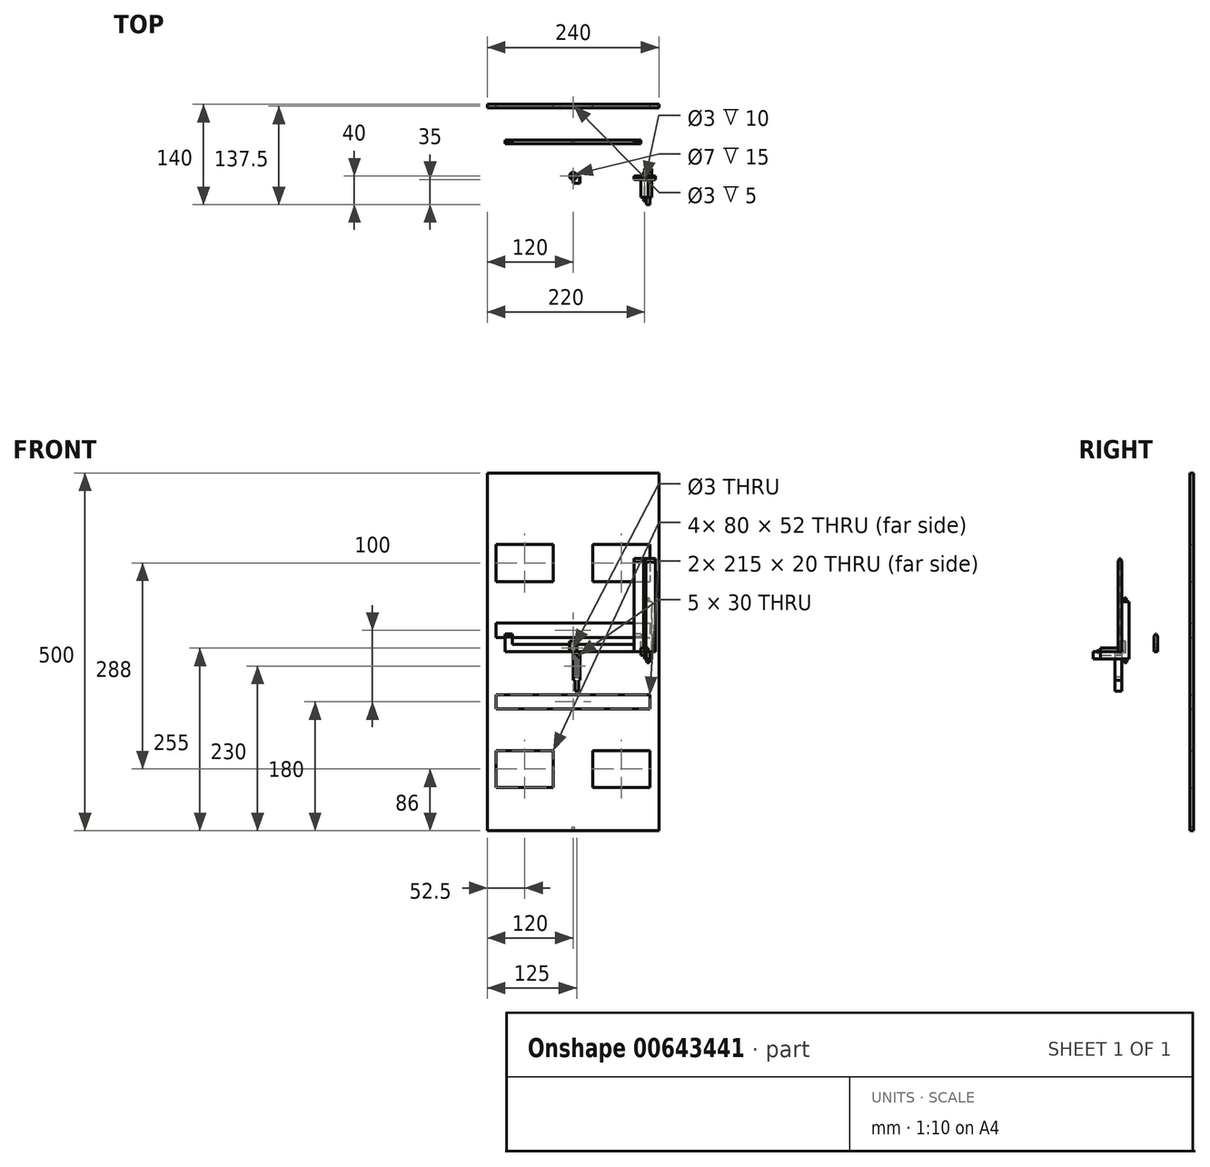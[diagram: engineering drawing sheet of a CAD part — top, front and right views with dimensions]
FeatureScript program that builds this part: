
annotation { "Feature Type Name" : "Feature", "Feature Type Description" : "" }
export const myFeature = defineFeature(function(context is Context, id is Id, definition is map)
    precondition{}
    {
        {
            var Q0;
            Q0=qCreatedBy(makeId("Front.planeOp"),FACE);
            var sketch = newSketch(context, id + "F0", { "sketchPlane" : qUnion([Q0])});
            skLineSegment(sketch, "E0", {"start": v(0, 0) * mm, "end": v(95, 0) * mm});
            skLineSegment(sketch, "E1", {"start": v(95, 0) * mm, "end": v(95, 25) * mm});
            skLineSegment(sketch, "E2", {"start": v(95, 25) * mm, "end": v(85, 25) * mm});
            skLineSegment(sketch, "E3", {"start": v(85, 25) * mm, "end": v(85, 10) * mm});
            skLineSegment(sketch, "E4", {"start": v(85, 10) * mm, "end": v(0, 10) * mm});
            skLineSegment(sketch, "E5.MirrorCS", {"start": v(-85, 25) * mm, "end": v(-85, 10) * mm});
            skLineSegment(sketch, "E6.MirrorCS", {"start": v(-85, 10) * mm, "end": v(0, 10) * mm});
            skLineSegment(sketch, "E7.MirrorCS", {"start": v(-95, 0) * mm, "end": v(-95, 25) * mm});
            skLineSegment(sketch, "E8.MirrorCS", {"start": v(0, 0) * mm, "end": v(-95, 0) * mm});
            skLineSegment(sketch, "E9.MirrorCS", {"start": v(-95, 25) * mm, "end": v(-85, 25) * mm});
            skCircle(sketch, "E10", {"center": v(0, 5) * mm, "radius": 1.5 * mm});
            skSolve(sketch);
        }
        {
            var Q0;
            Q0=makeQuery(id+"F0.imprint","IMPRINT",FACE,{"disambiguationData":[TD([[makeQuery(id+"F0.imprint","IMPRINT",EDGE,{"derivedFrom":sQuery(id+"F0.wireOp",EDGE,"E0")}),1.0]])]});
            extrude(context, id + "F1", {"entities" : qUnion([Q0]), "depth" : 5 * mm, "offsetDistance" : 25 * mm});
        }
        {
            var Q0;
            Q0=makeQuery(id+"F1.opExtrude","CAP_EDGE",EDGE,{"disambiguationData":[OSD([sQuery(id+"F0.wireOp",EDGE,"E2")])],"isStart":false});
            var Q1;
            Q1=makeQuery(id+"F1.opExtrude","CAP_EDGE",EDGE,{"disambiguationData":[OSD([sQuery(id+"F0.wireOp",EDGE,"E9.MirrorCS")])],"isStart":false});
            var Q2;
            Q2=makeQuery(id+"F1.opExtrude","CAP_EDGE",EDGE,{"disambiguationData":[OSD([sQuery(id+"F0.wireOp",EDGE,"E2")])],"isStart":true});
            var Q3;
            Q3=makeQuery(id+"F1.opExtrude","CAP_EDGE",EDGE,{"disambiguationData":[OSD([sQuery(id+"F0.wireOp",EDGE,"E9.MirrorCS")])],"isStart":true});
            chamfer(context, id + "F2", {"entities" : qUnion([Q0, Q1, Q2, Q3]), "chamferType" : ChamferType.TWO_OFFSETS, "width1" : 4 * mm, "oppositeDirection" : false, "width2" : 2 * mm, "tangentPropagation" : true});
        }
        {
            var Q0;
            Q0=makeQuery(id+"F1.opExtrude","SWEPT_BODY",BODY,{"disambiguationData":[OSD([sQuery(id+"F0.wireOp",EDGE,"E0"),sQuery(id+"F0.wireOp",EDGE,"E1"),sQuery(id+"F0.wireOp",EDGE,"E2"),sQuery(id+"F0.wireOp",EDGE,"E3"),sQuery(id+"F0.wireOp",EDGE,"E4"),sQuery(id+"F0.wireOp",EDGE,"E5.MirrorCS"),sQuery(id+"F0.wireOp",EDGE,"E6.MirrorCS"),sQuery(id+"F0.wireOp",EDGE,"E7.MirrorCS"),sQuery(id+"F0.wireOp",EDGE,"E8.MirrorCS"),sQuery(id+"F0.wireOp",EDGE,"E9.MirrorCS")])]});
            transform(context, id + "F3", {"entities" : qUnion([Q0]), "transformType" : TransformType.TRANSLATION_3D, "dx" : 0 * mm, "dy" : 50 * mm, "dz" : 0 * mm, "makeCopy" : false});
        }
        {
            var Q0;
            Q0=qCreatedBy(makeId("Front.planeOp"),FACE);
            var sketch = newSketch(context, id + "F4", { "sketchPlane" : qUnion([Q0])});
            skLineSegment(sketch, "E11.bottom", {"start": v(-15, 0) * mm, "end": v(15, 0) * mm});
            skLineSegment(sketch, "E11.top", {"start": v(-15, 130) * mm, "end": v(15, 130) * mm});
            skLineSegment(sketch, "E11.left", {"start": v(-15, 0) * mm, "end": v(-15, 130) * mm});
            skLineSegment(sketch, "E11.right", {"start": v(15, 0) * mm, "end": v(15, 130) * mm});
            skCircle(sketch, "E12", {"center": v(0, 5) * mm, "radius": 1.5 * mm});
            skSolve(sketch);
        }
        {
            var Q0;
            Q0=makeQuery(id+"F4.imprint","IMPRINT",FACE,{"disambiguationData":[TD([[makeQuery(id+"F4.imprint","IMPRINT",EDGE,{"derivedFrom":sQuery(id+"F4.wireOp",EDGE,"E11.bottom")}),1.0]])]});
            extrude(context, id + "F5", {"entities" : qUnion([Q0]), "depth" : 5 * mm, "offsetDistance" : 25 * mm});
        }
        {
            var Q0;
            Q0=makeQuery(id+"F5.opExtrude","CAP_EDGE",EDGE,{"disambiguationData":[OSD([sQuery(id+"F4.wireOp",EDGE,"E11.top")])],"isStart":false});
            var Q1;
            Q1=makeQuery(id+"F5.opExtrude","CAP_EDGE",EDGE,{"disambiguationData":[OSD([sQuery(id+"F4.wireOp",EDGE,"E11.top")])],"isStart":true});
            chamfer(context, id + "F6", {"entities" : qUnion([Q0, Q1]), "chamferType" : ChamferType.TWO_OFFSETS, "width1" : 5 * mm, "oppositeDirection" : true, "width2" : 2 * mm, "tangentPropagation" : true});
        }
        {
            var Q0;
            Q0=qCreatedBy(makeId("Front.planeOp"),FACE);
            var sketch = newSketch(context, id + "F7", { "sketchPlane" : qUnion([Q0])});
            skLineSegment(sketch, "E13.bottom", {"start": v(-5, 5) * mm, "end": v(5, 5) * mm});
            skLineSegment(sketch, "E13.top", {"start": v(-5, -5) * mm, "end": v(5, -5) * mm});
            skLineSegment(sketch, "E13.left", {"start": v(-5, 5) * mm, "end": v(-5, -5) * mm});
            skLineSegment(sketch, "E13.right", {"start": v(5, 5) * mm, "end": v(5, -5) * mm});
            skSolve(sketch);
        }
        {
            var Q0;
            Q0=makeQuery(id+"F7.imprint","IMPRINT",FACE,{"disambiguationData":[TD([[makeQuery(id+"F7.imprint","IMPRINT",EDGE,{"derivedFrom":sQuery(id+"F7.wireOp",EDGE,"E13.bottom")}),-1.0]])]});
            extrude(context, id + "F8", {"entities" : qUnion([Q0]), "depth" : 30 * mm, "offsetDistance" : 25 * mm});
        }
        {
            var Q0;
            Q0=makeQuery(id+"F8.opExtrude","CAP_FACE",FACE,{"disambiguationData":[OSD([sQuery(id+"F7.wireOp",EDGE,"E13.bottom"),sQuery(id+"F7.wireOp",EDGE,"E13.top"),sQuery(id+"F7.wireOp",EDGE,"E13.left"),sQuery(id+"F7.wireOp",EDGE,"E13.right")])],"isStart":false});
            var sketch = newSketch(context, id + "F9", { "sketchPlane" : qUnion([Q0])});
            skCircle(sketch, "E14", {"center": v(0, 0) * mm, "radius": 1.5 * mm});
            skSolve(sketch);
        }
        {
            var Q0;
            Q0=makeQuery(id+"F9.imprint","IMPRINT",FACE,{"disambiguationData":[TD([[makeQuery(id+"F9.imprint","IMPRINT",EDGE,{"derivedFrom":sQuery(id+"F9.wireOp",EDGE,"E14")}),1.0]])]});
            extrude(context, id + "F10", {"entities" : qUnion([Q0]), "operationType" : NewBodyOperationType.ADD, "depth" : 5 * mm, "offsetDistance" : 25 * mm});
        }
        {
            var Q0;
            Q0=makeQuery(id+"F8.opExtrude","CAP_FACE",FACE,{"disambiguationData":[OSD([sQuery(id+"F7.wireOp",EDGE,"E13.bottom"),sQuery(id+"F7.wireOp",EDGE,"E13.top"),sQuery(id+"F7.wireOp",EDGE,"E13.left"),sQuery(id+"F7.wireOp",EDGE,"E13.right")])],"isStart":true});
            var sketch = newSketch(context, id + "F11", { "sketchPlane" : qUnion([Q0])});
            skCircle(sketch, "E15", {"center": v(0, 0) * mm, "radius": 1.5 * mm});
            skSolve(sketch);
        }
        {
            var Q0;
            Q0=makeQuery(id+"F11.imprint","IMPRINT",FACE,{"disambiguationData":[TD([[makeQuery(id+"F11.imprint","IMPRINT",EDGE,{"derivedFrom":sQuery(id+"F11.wireOp",EDGE,"E15")}),1.0]])]});
            extrude(context, id + "F12", {"entities" : qUnion([Q0]), "operationType" : NewBodyOperationType.ADD, "depth" : 5 * mm, "offsetDistance" : 25 * mm});
        }
        {
            var Q0;
            Q0=qCreatedBy(makeId("Right.planeOp"),FACE);
            var sketch = newSketch(context, id + "F13", { "sketchPlane" : qUnion([Q0])});
            skLineSegment(sketch, "E16", {"start": v(0, 70) * mm, "end": v(10, 70) * mm});
            skLineSegment(sketch, "E17", {"start": v(10, 70) * mm, "end": v(10, -10) * mm});
            skLineSegment(sketch, "E18", {"start": v(10, -10) * mm, "end": v(-30, -10) * mm});
            skLineSegment(sketch, "E19", {"start": v(-30, -10) * mm, "end": v(-30, 0) * mm});
            skLineSegment(sketch, "E20", {"start": v(-30, 0) * mm, "end": v(0, 0) * mm});
            skLineSegment(sketch, "E21", {"start": v(0, 0) * mm, "end": v(0, 15) * mm});
            skLineSegment(sketch, "E22", {"start": v(0, 20) * mm, "end": v(-5, 20) * mm});
            skLineSegment(sketch, "E23", {"start": v(-5, 20) * mm, "end": v(-5, 15) * mm});
            skLineSegment(sketch, "E24", {"start": v(-5, 15) * mm, "end": v(0, 15) * mm});
            skLineSegment(sketch, "E25.trimOffspring", {"start": v(0, 20) * mm, "end": v(0, 70) * mm});
            skSolve(sketch);
        }
        {
            var Q0;
            Q0=makeQuery(id+"F13.imprint","IMPRINT",FACE,{"disambiguationData":[TD([[makeQuery(id+"F13.imprint","IMPRINT",EDGE,{"derivedFrom":sQuery(id+"F13.wireOp",EDGE,"E16")}),-1.0]])]});
            extrude(context, id + "F14", {"entities" : qUnion([Q0]), "depth" : 10 * mm, "offsetDistance" : 25 * mm});
        }
        {
            var Q0;
            Q0=makeQuery(id+"F14.opExtrude","SWEPT_FACE",FACE,{"disambiguationData":[OSD([sQuery(id+"F13.wireOp",EDGE,"E16")])]});
            var sketch = newSketch(context, id + "F15", { "sketchPlane" : qUnion([Q0])});
            skCircle(sketch, "E26", {"center": v(5, 5) * mm, "radius": 1.5 * mm});
            skSolve(sketch);
        }
        {
            var Q0;
            Q0=makeQuery(id+"F15.imprint","IMPRINT",FACE,{"disambiguationData":[TD([[makeQuery(id+"F15.imprint","IMPRINT",EDGE,{"derivedFrom":sQuery(id+"F15.wireOp",EDGE,"E26")}),1.0]])]});
            extrude(context, id + "F16", {"entities" : qUnion([Q0]), "operationType" : NewBodyOperationType.ADD, "depth" : 5 * mm, "offsetDistance" : 25 * mm});
        }
        {
            var Q0;
            Q0=makeQuery(id+"F14.opExtrude","SWEPT_FACE",FACE,{"disambiguationData":[OSD([sQuery(id+"F13.wireOp",EDGE,"E19")])]});
            var sketch = newSketch(context, id + "F17", { "sketchPlane" : qUnion([Q0])});
            skLineSegment(sketch, "E27.bottom", {"start": v(2.5, 0) * mm, "end": v(7.5, 0) * mm});
            skLineSegment(sketch, "E27.top", {"start": v(2.5, -10) * mm, "end": v(7.5, -10) * mm});
            skLineSegment(sketch, "E27.left", {"start": v(2.5, 0) * mm, "end": v(2.5, -10) * mm});
            skLineSegment(sketch, "E27.right", {"start": v(7.5, 0) * mm, "end": v(7.5, -10) * mm});
            skSolve(sketch);
        }
        {
            var Q0;
            Q0=makeQuery(id+"F8.opExtrude","SWEPT_FACE",FACE,{"disambiguationData":[OSD([sQuery(id+"F7.wireOp",EDGE,"E13.top")])]});
            var sketch = newSketch(context, id + "F18", { "sketchPlane" : qUnion([Q0])});
            skCircle(sketch, "E28", {"center": v(0, 5) * mm, "radius": 1.5 * mm});
            skPoint(sketch, "E28.centerSnap0", {"position": v(0, 30) * mm});
            skSolve(sketch);
        }
        {
            var Q0;
            Q0=makeQuery(id+"F18.imprint","IMPRINT",FACE,{"disambiguationData":[TD([[makeQuery(id+"F18.imprint","IMPRINT",EDGE,{"derivedFrom":sQuery(id+"F18.wireOp",EDGE,"E28")}),1.0]])]});
            extrude(context, id + "F19", {"entities" : qUnion([Q0]), "operationType" : NewBodyOperationType.REMOVE, "endBound" : BoundingType.THROUGH_ALL, "oppositeDirection" : true, "depth" : 5 * mm, "offsetDistance" : 25 * mm});
        }
        {
            var Q0;
            Q0=makeQuery(id+"F17.imprint","IMPRINT",FACE,{"disambiguationData":[TD([[makeQuery(id+"F17.imprint","IMPRINT",EDGE,{"derivedFrom":sQuery(id+"F17.wireOp",EDGE,"E27.bottom")}),1.0]])]});
            extrude(context, id + "F20", {"entities" : qUnion([Q0]), "operationType" : NewBodyOperationType.ADD, "depth" : 10 * mm, "offsetDistance" : 25 * mm});
        }
        {
            var Q0;
            Q0=qCreatedBy(makeId("Front.planeOp"),FACE);
            var sketch = newSketch(context, id + "F21", { "sketchPlane" : qUnion([Q0])});
            skLineSegment(sketch, "E29", {"start": v(0, 0) * mm, "end": v(10, 0) * mm});
            skLineSegment(sketch, "E30", {"start": v(10, 0) * mm, "end": v(10, -40) * mm});
            skLineSegment(sketch, "E31", {"start": v(10, -40) * mm, "end": v(7.5, -40) * mm});
            skLineSegment(sketch, "E32", {"start": v(7.5, -40) * mm, "end": v(7.5, -55) * mm});
            skLineSegment(sketch, "E33", {"start": v(7.5, -55) * mm, "end": v(2.5, -55) * mm});
            skLineSegment(sketch, "E34", {"start": v(2.5, -55) * mm, "end": v(2.5, -40) * mm});
            skLineSegment(sketch, "E35", {"start": v(2.5, -40) * mm, "end": v(0, -40) * mm});
            skLineSegment(sketch, "E36", {"start": v(0, -40) * mm, "end": v(0, 0) * mm});
            skLineSegment(sketch, "E37.bottom", {"start": v(2.5, -5) * mm, "end": v(7.5, -5) * mm});
            skLineSegment(sketch, "E37.top", {"start": v(2.5, -35) * mm, "end": v(7.5, -35) * mm});
            skLineSegment(sketch, "E37.left", {"start": v(2.5, -5) * mm, "end": v(2.5, -35) * mm});
            skLineSegment(sketch, "E37.right", {"start": v(7.5, -5) * mm, "end": v(7.5, -35) * mm});
            skSolve(sketch);
        }
        {
            var Q0;
            Q0=makeQuery(id+"F21.imprint","IMPRINT",FACE,{"disambiguationData":[TD([[makeQuery(id+"F21.imprint","IMPRINT",EDGE,{"derivedFrom":sQuery(id+"F21.wireOp",EDGE,"E29")}),-1.0]])]});
            extrude(context, id + "F22", {"entities" : qUnion([Q0]), "depth" : 10 * mm, "offsetDistance" : 25 * mm});
        }
        {
            var Q0;
            Q0=qCreatedBy(makeId("Front.planeOp"),FACE);
            var sketch = newSketch(context, id + "F23", { "sketchPlane" : qUnion([Q0])});
            skLineSegment(sketch, "E38.bottom", {"start": v(-120, 250) * mm, "end": v(120, 250) * mm});
            skLineSegment(sketch, "E38.top", {"start": v(-120, -250) * mm, "end": v(120, -250) * mm});
            skLineSegment(sketch, "E38.left", {"start": v(-120, 250) * mm, "end": v(-120, -250) * mm});
            skLineSegment(sketch, "E38.right", {"start": v(120, 250) * mm, "end": v(120, -250) * mm});
            skLineSegment(sketch, "E39.bottom", {"start": v(-107.5, -138) * mm, "end": v(-27.5, -138) * mm});
            skLineSegment(sketch, "E39.top", {"start": v(-107.5, -190) * mm, "end": v(-27.5, -190) * mm});
            skLineSegment(sketch, "E39.left", {"start": v(-107.5, -138) * mm, "end": v(-107.5, -190) * mm});
            skLineSegment(sketch, "E39.right", {"start": v(-27.5, -138) * mm, "end": v(-27.5, -190) * mm});
            skLineSegment(sketch, "E40.bottom", {"start": v(-107.5, -60) * mm, "end": v(107.5, -60) * mm});
            skLineSegment(sketch, "E40.top", {"start": v(-107.5, -80) * mm, "end": v(107.5, -80) * mm});
            skLineSegment(sketch, "E40.left", {"start": v(-107.5, -60) * mm, "end": v(-107.5, -80) * mm});
            skLineSegment(sketch, "E40.right", {"start": v(107.5, -60) * mm, "end": v(107.5, -80) * mm});
            skLineSegment(sketch, "E41.bottom", {"start": v(27.5, -138) * mm, "end": v(107.5, -138) * mm});
            skLineSegment(sketch, "E41.top", {"start": v(27.5, -190) * mm, "end": v(107.5, -190) * mm});
            skLineSegment(sketch, "E41.left", {"start": v(27.5, -138) * mm, "end": v(27.5, -190) * mm});
            skLineSegment(sketch, "E41.right", {"start": v(107.5, -138) * mm, "end": v(107.5, -190) * mm});
            skLineSegment(sketch, "E42.bottom", {"start": v(-107.5, 40) * mm, "end": v(107.5, 40) * mm});
            skLineSegment(sketch, "E42.top", {"start": v(-107.5, 20) * mm, "end": v(107.5, 20) * mm});
            skLineSegment(sketch, "E42.left", {"start": v(-107.5, 40) * mm, "end": v(-107.5, 20) * mm});
            skLineSegment(sketch, "E42.right", {"start": v(107.5, 40) * mm, "end": v(107.5, 20) * mm});
            skLineSegment(sketch, "E43.bottom", {"start": v(-107.5, 150) * mm, "end": v(-27.5, 150) * mm});
            skLineSegment(sketch, "E43.top", {"start": v(-107.5, 98) * mm, "end": v(-27.5, 98) * mm});
            skLineSegment(sketch, "E43.left", {"start": v(-107.5, 150) * mm, "end": v(-107.5, 98) * mm});
            skLineSegment(sketch, "E43.right", {"start": v(-27.5, 150) * mm, "end": v(-27.5, 98) * mm});
            skLineSegment(sketch, "E44.bottom", {"start": v(27.5, 150) * mm, "end": v(107.5, 150) * mm});
            skLineSegment(sketch, "E44.top", {"start": v(27.5, 98) * mm, "end": v(107.5, 98) * mm});
            skLineSegment(sketch, "E44.left", {"start": v(27.5, 150) * mm, "end": v(27.5, 98) * mm});
            skLineSegment(sketch, "E44.right", {"start": v(107.5, 150) * mm, "end": v(107.5, 98) * mm});
            skSolve(sketch);
        }
        {
            var Q0;
            Q0=makeQuery(id+"F23.imprint","IMPRINT",FACE,{"disambiguationData":[TD([[makeQuery(id+"F23.imprint","IMPRINT",EDGE,{"derivedFrom":sQuery(id+"F23.wireOp",EDGE,"E38.bottom")}),-1.0]])]});
            extrude(context, id + "F24", {"entities" : qUnion([Q0]), "depth" : 5 * mm, "offsetDistance" : 25 * mm});
        }
        {
            var Q0;
            Q0=makeQuery(id+"F24.opExtrude","SWEPT_FACE",FACE,{"disambiguationData":[OSD([sQuery(id+"F23.wireOp",EDGE,"E38.top")])]});
            var sketch = newSketch(context, id + "F25", { "sketchPlane" : qUnion([Q0])});
            skCircle(sketch, "E45", {"center": v(0, 2.5) * mm, "radius": 1.5 * mm});
            skSolve(sketch);
        }
        {
            var Q0;
            Q0=makeQuery(id+"F25.imprint","IMPRINT",FACE,{"disambiguationData":[TD([[makeQuery(id+"F25.imprint","IMPRINT",EDGE,{"derivedFrom":sQuery(id+"F25.wireOp",EDGE,"E45")}),1.0]])]});
            extrude(context, id + "F26", {"entities" : qUnion([Q0]), "operationType" : NewBodyOperationType.REMOVE, "oppositeDirection" : true, "depth" : 5 * mm, "offsetDistance" : 25 * mm});
        }
        {
            var Q0;
            Q0=makeQuery(id+"F20.boolean.opBoolean","MERGE",FACE,{"derivedFrom":[makeQuery(id+"F14.opExtrude","SWEPT_FACE",FACE,{"disambiguationData":[OSD([sQuery(id+"F13.wireOp",EDGE,"E18")])]}),makeQuery(id+"F20.opExtrude","SWEPT_FACE",FACE,{"disambiguationData":[OSD([sQuery(id+"F17.wireOp",EDGE,"E27.top")])]})]});
            var sketch = newSketch(context, id + "F27", { "sketchPlane" : qUnion([Q0])});
            skCircle(sketch, "E46", {"center": v(5, -5) * mm, "radius": 2 * mm});
            skSolve(sketch);
        }
        {
            var Q0;
            Q0=makeQuery(id+"F27.imprint","IMPRINT",FACE,{"disambiguationData":[TD([[makeQuery(id+"F27.imprint","IMPRINT",EDGE,{"derivedFrom":sQuery(id+"F27.wireOp",EDGE,"E46")}),1.0]])]});
            extrude(context, id + "F28", {"entities" : qUnion([Q0]), "operationType" : NewBodyOperationType.ADD, "depth" : 5 * mm, "offsetDistance" : 25 * mm});
        }
        {
            var Q0;
            Q0=makeQuery(id+"F24.opExtrude","SWEPT_BODY",BODY,{"disambiguationData":[OSD([sQuery(id+"F23.wireOp",EDGE,"E38.bottom"),sQuery(id+"F23.wireOp",EDGE,"E38.top"),sQuery(id+"F23.wireOp",EDGE,"E38.left"),sQuery(id+"F23.wireOp",EDGE,"E38.right"),sQuery(id+"F23.wireOp",EDGE,"E39.bottom"),sQuery(id+"F23.wireOp",EDGE,"E39.top"),sQuery(id+"F23.wireOp",EDGE,"E39.left"),sQuery(id+"F23.wireOp",EDGE,"E39.right"),sQuery(id+"F23.wireOp",EDGE,"E40.bottom"),sQuery(id+"F23.wireOp",EDGE,"E40.top"),sQuery(id+"F23.wireOp",EDGE,"E40.left"),sQuery(id+"F23.wireOp",EDGE,"E40.right"),sQuery(id+"F23.wireOp",EDGE,"E41.bottom"),sQuery(id+"F23.wireOp",EDGE,"E41.top"),sQuery(id+"F23.wireOp",EDGE,"E41.left"),sQuery(id+"F23.wireOp",EDGE,"E41.right"),sQuery(id+"F23.wireOp",EDGE,"E42.bottom"),sQuery(id+"F23.wireOp",EDGE,"E42.top"),sQuery(id+"F23.wireOp",EDGE,"E42.left"),sQuery(id+"F23.wireOp",EDGE,"E42.right"),sQuery(id+"F23.wireOp",EDGE,"E43.bottom"),sQuery(id+"F23.wireOp",EDGE,"E43.top"),sQuery(id+"F23.wireOp",EDGE,"E43.left"),sQuery(id+"F23.wireOp",EDGE,"E43.right"),sQuery(id+"F23.wireOp",EDGE,"E44.bottom"),sQuery(id+"F23.wireOp",EDGE,"E44.top"),sQuery(id+"F23.wireOp",EDGE,"E44.left"),sQuery(id+"F23.wireOp",EDGE,"E44.right")])]});
            transform(context, id + "F29", {"entities" : qUnion([Q0]), "transformType" : TransformType.TRANSLATION_3D, "dx" : 0 * mm, "dy" : 100 * mm, "dz" : 0 * mm, "makeCopy" : false});
        }
        {
            var Q0;
            Q0=makeQuery(id+"F5.opExtrude","SWEPT_BODY",BODY,{"disambiguationData":[OSD([sQuery(id+"F4.wireOp",EDGE,"E11.bottom"),sQuery(id+"F4.wireOp",EDGE,"E11.top"),sQuery(id+"F4.wireOp",EDGE,"E11.left"),sQuery(id+"F4.wireOp",EDGE,"E11.right"),sQuery(id+"F4.wireOp",EDGE,"E12")])]});
            transform(context, id + "F30", {"entities" : qUnion([Q0]), "transformType" : TransformType.TRANSLATION_3D, "dx" : 100 * mm, "dy" : 0 * mm, "dz" : 0 * mm, "makeCopy" : false});
        }
        {
            var Q0;
            Q0=qCreatedBy(makeId("Top.planeOp"),FACE);
            var sketch = newSketch(context, id + "F31", { "sketchPlane" : qUnion([Q0])});
            skCircle(sketch, "E47", {"center": v(0, 0) * mm, "radius": 5 * mm});
            skCircle(sketch, "E48", {"center": v(0, 0) * mm, "radius": 3.5 * mm});
            skSolve(sketch);
        }
        {
            var Q0;
            Q0=makeQuery(id+"F31.imprint","IMPRINT",FACE,{"disambiguationData":[TD([[makeQuery(id+"F31.imprint","IMPRINT",EDGE,{"derivedFrom":sQuery(id+"F31.wireOp",EDGE,"E47")}),1.0]])]});
            extrude(context, id + "F32", {"entities" : qUnion([Q0]), "depth" : 15 * mm, "offsetDistance" : 25 * mm});
        }
    });
